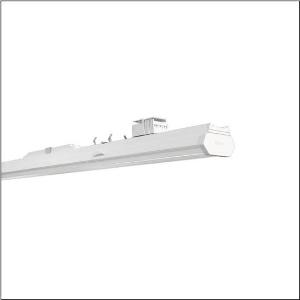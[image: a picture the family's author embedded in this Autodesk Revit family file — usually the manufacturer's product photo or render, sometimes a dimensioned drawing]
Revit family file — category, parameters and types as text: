
# Revit family: licross_r__11_protected_mo_51tp12dn495g_6914
name_source: partatom
category: Lighting Fixtures
units: mm (PartAtom-declared; Revit-internal decimal feet)

## family parameters
Cut with Voids When Loaded = No
Host = Face
Light Source = No
Part Type = Normal
Room Calculation Point = No
Round Connector Dimension = Use Diameter
Shared = No

## types (1)
- --- (1 x LED, 9980 lm, 57.1 W, 4000K)
    Apparent Load = 57 VA
    CIE Flux Codes = 73 92 98 99 100
    Color Rendering = 80
    Color Temperature = 4000K
    Default Elevation = 1800 mm
    Description = Licross® 11 Protected MO, luminaire insert, of sheet steel, galvanised, coil coated, white, length: 1.500mm, width: 90mm, height: 101mm, LED rated luminous flux: 9.980lm, light colour: 840, control gear: DALI 2, with plug, 5-pole, with phase selection, mains connection: 220..240V, AC, 50/60Hz, rated input power: 57W, halogen-free wiring, primary optical cover: cover, of PMMA, light emission: direct distribution, primary light characteristic: symmetric, protection rating (complete): IP64, insulation class (complete): insulation class I (protective earthing), certification: CE, ENEC, VDE, UKCA, protection symbol: D if used in an environment with conductive dust loads with corresponding accessories, impact resistance: IK06, permissible ambient temperature for indoor applications: -25..+35°C, corresponds to IFS (International Featured Standards) requirements for safety and quality in the food industry, reducing of maximum allowable ambient temperature of 5°C with ceiling mounting, LABS conformity tested according to VDMA 24364:2018-05, packaging unit: 1 piece
    Height = 92 mm
    Lamp = 1 x LED
    Lamp Light Flux = 9980 lm
    Lamp Power = 57.1 W
    Lamp count = 1
    Length = 1500 mm
    Luminous efficacy = 175 lm/W
    Manufacturer = Siteco
    ModVariant = No
    Model = 51TP12DN495G
    Mounting Place = Ceiling
    Mounting Type = Pendant
    Number of Poles = 1
    OnlyDefault = Yes
    Power Factor = 1
    Product Name = Licross® 11 Protected MO
    Product group = luminaire insert
    ProductGroupID = 901
    Protection Class = Protection class I
    Protection Degree = IP 64
    RLX_Detail_Level = 1
    RLX_Emergency_Light_Flux = 0 lm
    RLX_Emergency_Type = 0
    RLX_Emergency_Type_DB = No
    RlxData = <blob elided: 24317 chars, md5=c32a8369>
    Socket = socket
    Standby Power = 0 W
    System Light Flux = 9980 lm
    System Power = 57 W
    Type Comments = factory setting: luminous flux: 100 % | dim-lin: 254 | 378 mA
    Type Image = l_1256148.jpg
    URL = http://relux.com
    VarID = @adj_069987
    Voltage = 0 V
    Weight = 0.00 kg
    Width = 88 mm

## geometry (parser evidence)
native form markers: Blend x4, Sweep x10
no freeform markers — native parametric forms only
